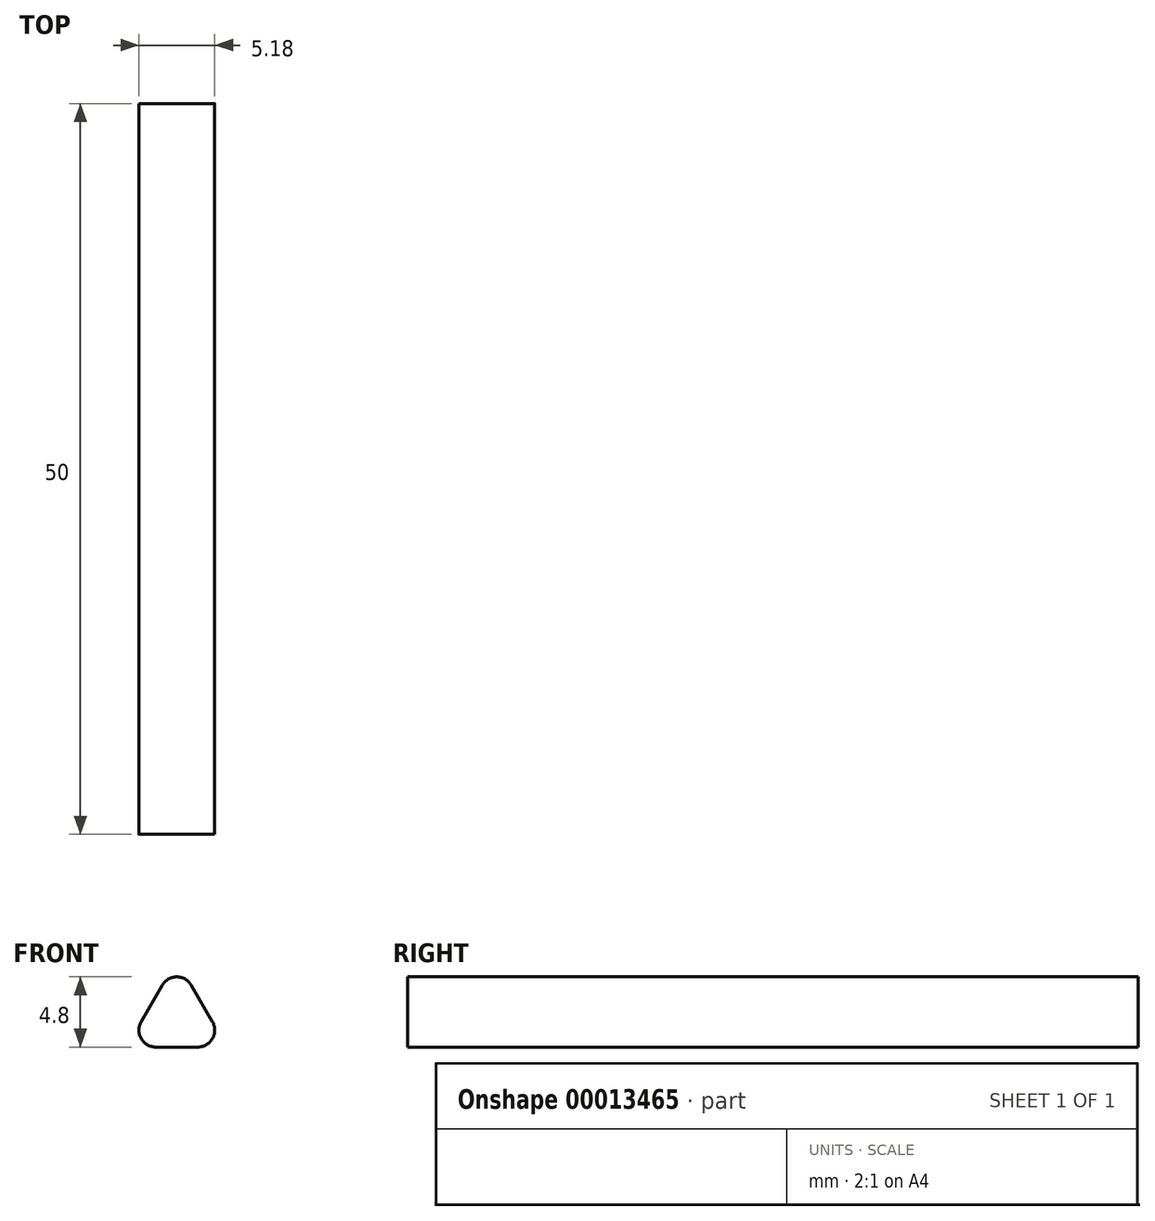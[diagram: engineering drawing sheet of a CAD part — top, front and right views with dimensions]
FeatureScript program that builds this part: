
annotation { "Feature Type Name" : "Feature", "Feature Type Description" : "" }
export const myFeature = defineFeature(function(context is Context, id is Id, definition is map)
    precondition{}
    {
        {
            var Q0;
            Q0=qCreatedBy(makeId("Front.planeOp"),FACE);
            var sketch = newSketch(context, id + "F0", { "sketchPlane" : qUnion([Q0])});
            skLineSegment(sketch, "E0", {"start": v(-1.44, 0) * mm, "end": v(1.44, 0) * mm});
            skArc(sketch, "E1", {"start": v(-1.44, 0) * mm, "mid": v(-2.44, 0.58) * mm, "end": v(-2.44, 1.73) * mm});
            skArc(sketch, "E2", {"start": v(1.44, 0) * mm, "mid": v(2.44, 0.58) * mm, "end": v(2.44, 1.73) * mm});
            skLineSegment(sketch, "E3", {"start": v(-2.44, 1.73) * mm, "end": v(-1, 4.22) * mm});
            skLineSegment(sketch, "E4", {"start": v(2.44, 1.73) * mm, "end": v(1, 4.22) * mm});
            skArc(sketch, "E5", {"start": v(1, 4.22) * mm, "mid": v(0, 4.8) * mm, "end": v(-1, 4.22) * mm});
            skSolve(sketch);
        }
        {
            var Q0;
            Q0=makeQuery(id+"F0.imprint","IMPRINT",FACE,{"disambiguationData":[TD([[makeQuery(id+"F0.imprint","IMPRINT",EDGE,{"derivedFrom":sQuery(id+"F0.wireOp",EDGE,"E0")}),1.0]])]});
            extrude(context, id + "F1", {"entities" : qUnion([Q0]), "depth" : 50 * mm});
        }
    });
